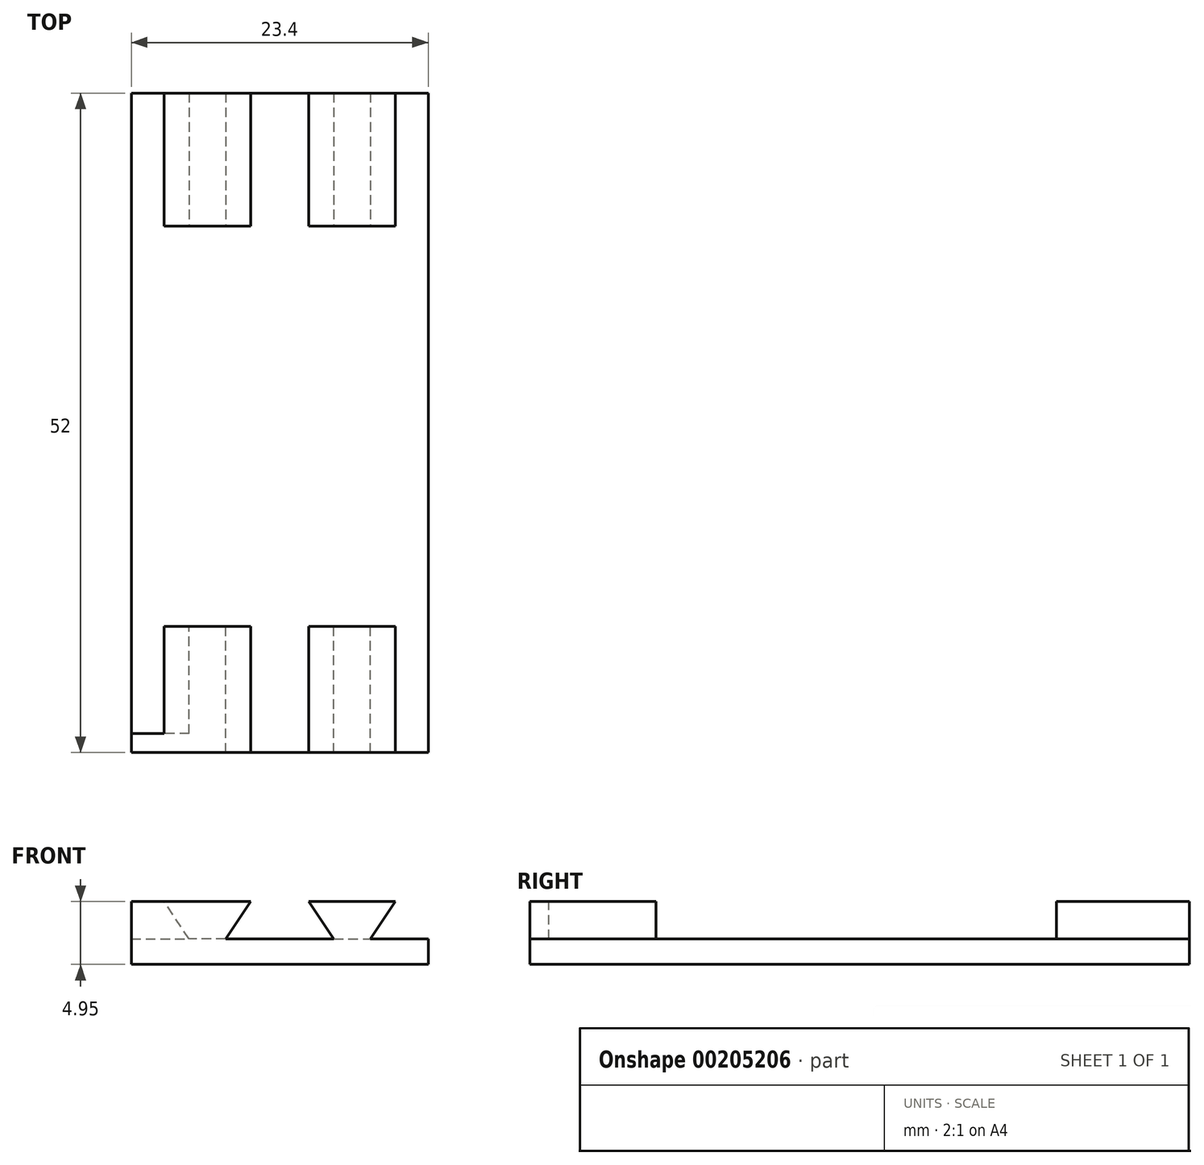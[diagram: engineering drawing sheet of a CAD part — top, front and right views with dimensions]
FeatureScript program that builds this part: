
annotation { "Feature Type Name" : "Feature", "Feature Type Description" : "" }
export const myFeature = defineFeature(function(context is Context, id is Id, definition is map)
    precondition{}
    {
        {
            var Q0;
            Q0=qCreatedBy(makeId("Top.planeOp"),FACE);
            var sketch = newSketch(context, id + "F0", { "sketchPlane" : qUnion([Q0])});
            skLineSegment(sketch, "E0", {"start": v(-11.7, 27) * mm, "end": v(-11.7, -25) * mm});
            skLineSegment(sketch, "E1", {"start": v(-11.7, -25) * mm, "end": v(11.7, -25) * mm});
            skLineSegment(sketch, "E2", {"start": v(11.7, -25) * mm, "end": v(11.7, 27) * mm});
            skLineSegment(sketch, "E3", {"start": v(-11.7, 27) * mm, "end": v(11.7, 27) * mm});
            skSolve(sketch);
        }
        {
            var Q0;
            Q0=makeQuery(id+"F0.imprint","IMPRINT",FACE,{"disambiguationData":[TD([[makeQuery(id+"F0.imprint","IMPRINT",EDGE,{"derivedFrom":sQuery(id+"F0.wireOp",EDGE,"E0")}),1.0]])]});
            extrude(context, id + "F1", {"entities" : qUnion([Q0]), "depth" : 2 * mm});
        }
        {
            var Q0;
            Q0=qCreatedBy(makeId("Front.planeOp"),FACE);
            var sketch = newSketch(context, id + "F2", { "sketchPlane" : qUnion([Q0])});
            skLineSegment(sketch, "E4", {"start": v(0, 0) * mm, "end": v(0, 5) * mm, "construction": true});
            skLineSegment(sketch, "E5.0", {"start": v(7.2, 2) * mm, "end": v(9.2, 5) * mm, "construction": true});
            skLineSegment(sketch, "E6.trimOffspring", {"start": v(2.2, 5) * mm, "end": v(4.2, 2) * mm, "construction": true});
            skLineSegment(sketch, "E7", {"start": v(4.2, 2) * mm, "end": v(7.2, 2) * mm});
            skLineSegment(sketch, "E8", {"start": v(2.2, 5) * mm, "end": v(9.2, 5) * mm, "construction": true});
            skLineSegment(sketch, "E9", {"start": v(0, 5) * mm, "end": v(0, 11.66) * mm, "construction": true});
            skLineSegment(sketch, "E10.MirrorCS", {"start": v(-2.2, 5) * mm, "end": v(-4.2, 2) * mm, "construction": true});
            skLineSegment(sketch, "E11.MirrorCS", {"start": v(-2.2, 5) * mm, "end": v(-9.2, 5) * mm, "construction": true});
            skLineSegment(sketch, "E12.MirrorCS", {"start": v(-7.2, 2) * mm, "end": v(-9.2, 5) * mm, "construction": true});
            skLineSegment(sketch, "E13.MirrorCS", {"start": v(-4.2, 2) * mm, "end": v(-7.2, 2) * mm, "construction": true});
            skPoint(sketch, "E14", {"position": v(-5.7, 5) * mm});
            skPoint(sketch, "E15", {"position": v(5.7, 5) * mm});
            skLineSegment(sketch, "E16.0", {"start": v(7.14, 2) * mm, "end": v(9.1, 4.95) * mm});
            skLineSegment(sketch, "E17.trimOffspring", {"start": v(2.3, 4.95) * mm, "end": v(9.1, 4.95) * mm});
            skLineSegment(sketch, "E18.trimOffspring", {"start": v(2.3, 4.95) * mm, "end": v(4.26, 2) * mm});
            skLineSegment(sketch, "E19.MirrorCS", {"start": v(-2.3, 4.95) * mm, "end": v(-4.26, 2) * mm});
            skLineSegment(sketch, "E20.MirrorCS", {"start": v(-2.3, 4.95) * mm, "end": v(-9.1, 4.95) * mm});
            skLineSegment(sketch, "E21.MirrorCS", {"start": v(-7.14, 2) * mm, "end": v(-9.1, 4.95) * mm});
            skLineSegment(sketch, "E22", {"start": v(7.14, 2) * mm, "end": v(4.26, 2) * mm});
            skLineSegment(sketch, "E23", {"start": v(-4.26, 2) * mm, "end": v(-7.14, 2) * mm});
            skSolve(sketch);
        }
        {
            var Q0;
            Q0 = qSketchRegion(id + "F2", true);
            extrude(context, id + "F3", {"entities" : qUnion([Q0]), "operationType" : NewBodyOperationType.ADD, "depth" : 25 * mm, "hasSecondDirection" : true, "secondDirectionOppositeDirection" : false, "secondDirectionDepth" : 15.05 * mm});
        }
        {
            var Q0;
            Q0=makeQuery(id+"F1.opExtrude","CAP_FACE",FACE,{"disambiguationData":[OSD([sQuery(id+"F0.wireOp",EDGE,"E0"),sQuery(id+"F0.wireOp",EDGE,"E1"),sQuery(id+"F0.wireOp",EDGE,"E2"),sQuery(id+"F0.wireOp",EDGE,"E3")])],"isStart":false});
            var sketch = newSketch(context, id + "F4", { "sketchPlane" : qUnion([Q0])});
            skLineSegment(sketch, "E24", {"start": v(11.7, -25) * mm, "end": v(11.7, -23.5) * mm});
            skLineSegment(sketch, "E25", {"start": v(11.7, -23.5) * mm, "end": v(-11.7, -23.5) * mm});
            skLineSegment(sketch, "E26.bottom", {"start": v(-11.7, -23.5) * mm, "end": v(11.7, -23.5) * mm});
            skLineSegment(sketch, "E26.top", {"start": v(-11.7, -25) * mm, "end": v(11.7, -25) * mm});
            skLineSegment(sketch, "E26.left", {"start": v(-11.7, -23.5) * mm, "end": v(-11.7, -25) * mm});
            skLineSegment(sketch, "E26.right", {"start": v(11.7, -23.5) * mm, "end": v(11.7, -25) * mm});
            skSolve(sketch);
        }
        {
            var Q0;
            {var subQ0=sQuery(id+"F4.wireOp",EDGE,"E26.bottom");var subQ1=makeQuery(id+"F3.opExtrude","SWEPT_EDGE",EDGE,{"disambiguationData":[OSD([sQuery(id+"F2.wireOp",EDGE,"E10.MirrorCS"),sQuery(id+"F2.wireOp",EDGE,"E13.MirrorCS")])]});var subQ2=makeQuery(id+"F4.imprint","INTERSECT",VERTEX,{"derivedFrom":[subQ1,subQ0]});Q0=makeQuery(id+"F4.imprint","IMPRINT",FACE,{"disambiguationData":[TD([[makeQuery(id+"F4.imprint","IMPRINT",EDGE,{"disambiguationData":[TD([[subQ2,-1.0]])],"derivedFrom":subQ0}),-1.0]])]});}
            var Q1;
            {var subQ0=sQuery(id+"F4.wireOp",EDGE,"E26.left");Q1=makeQuery(id+"F4.imprint","IMPRINT",FACE,{"disambiguationData":[TD([[makeQuery(id+"F4.imprint","IMPRINT",EDGE,{"derivedFrom":subQ0}),1.0]])]});}
            var Q2;
            {var subQ0=sQuery(id+"F4.wireOp",EDGE,"E26.right");Q2=makeQuery(id+"F4.imprint","IMPRINT",FACE,{"disambiguationData":[TD([[makeQuery(id+"F4.imprint","IMPRINT",EDGE,{"derivedFrom":subQ0}),1.0]])]});}
            extrude(context, id + "F5", {"entities" : qUnion([Q0, Q1, Q2]), "operationType" : NewBodyOperationType.ADD, "depth" : 2.95 * mm});
        }
        {
            var Q0;
            Q0 = qSketchRegion(id + "F2", true);
            extrude(context, id + "F6", {"entities" : qUnion([Q0]), "operationType" : NewBodyOperationType.ADD, "oppositeDirection" : true, "depth" : 27 * mm, "hasSecondDirection" : true, "secondDirectionOppositeDirection" : true, "secondDirectionDepth" : 16.5 * mm});
        }
    });
